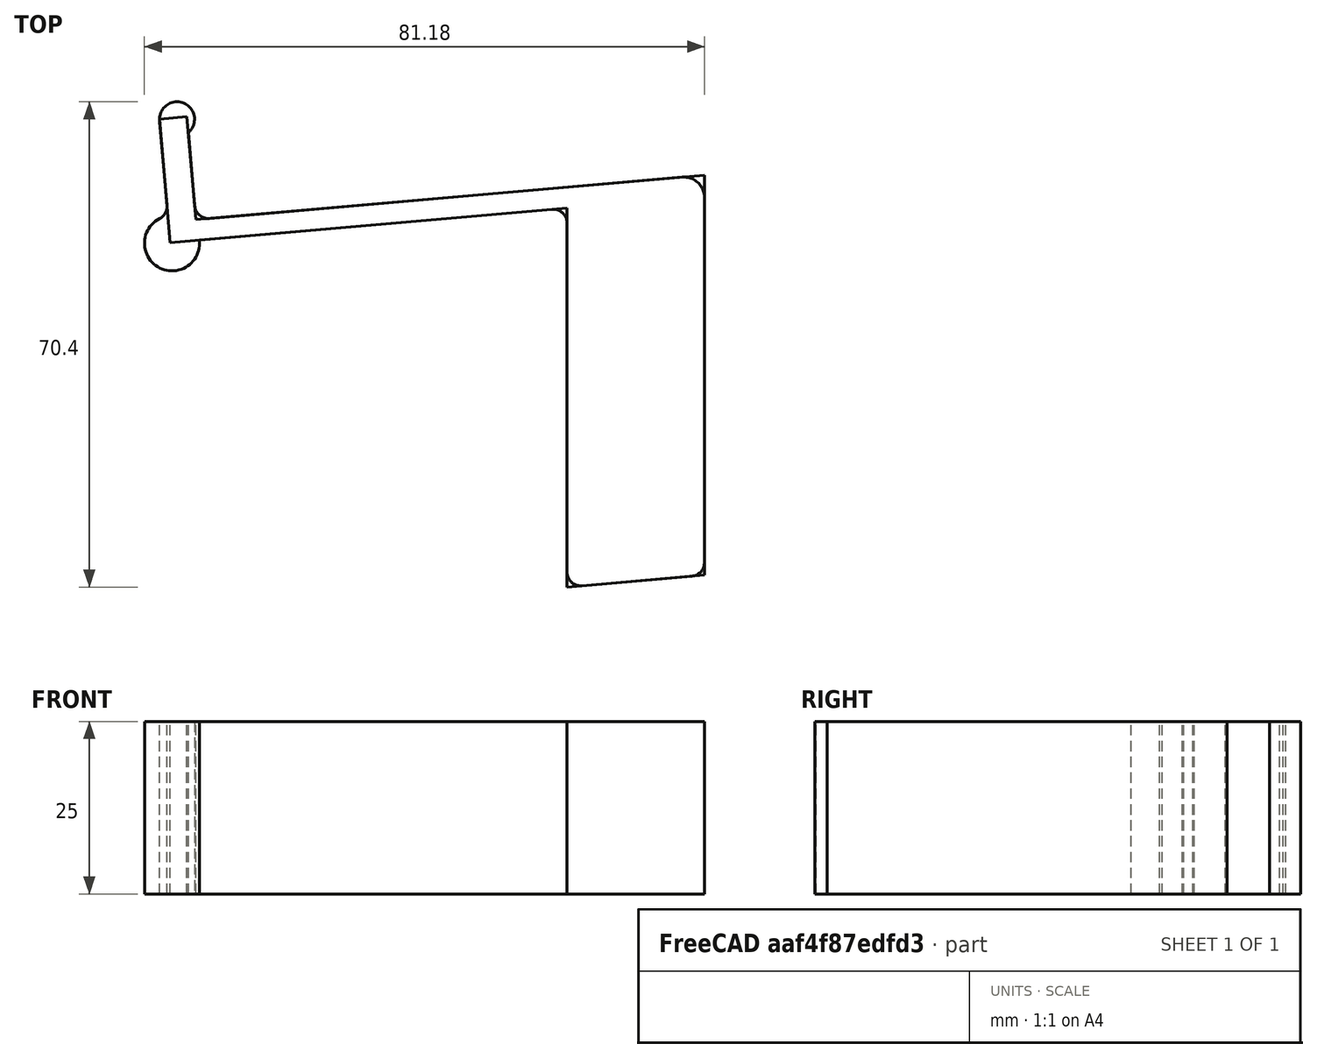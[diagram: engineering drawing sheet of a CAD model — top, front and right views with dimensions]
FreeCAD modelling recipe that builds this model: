
FCSTD DOCUMENT  (FreeCAD 0.16R)
Label: Hooks6
License: All rights reserved
LicenseURL: http://en.wikipedia.org/wiki/All_rights_reserved
objects: Sketcher::SketchObject×2, PartDesign::Pad×2, PartDesign::Fillet×2, Mesh::Feature×1
note: 8 computed .brp shape members not serialized (recipe doc carries the construction recipe); baked Part::Feature solids carry a one-line shape summary decoded from their .brp

FEATURE [Sketcher::SketchObject] Sketch
  sketch-geometry (9):
    g0: LineSegment StartX=19.9229 StartY=1.75449 StartZ=0 EndX=0 EndY=0 EndZ=0
    g1: LineSegment StartX=0 StartY=0 StartZ=0 EndX=0 EndY=55 EndZ=0
    g2: LineSegment StartX=0 StartY=55 StartZ=0 EndX=-57.5188 EndY=49.9678 EndZ=0
    g3: LineSegment StartX=-57.5188 StartY=49.9678 StartZ=0 EndX=-59.0876 EndY=67.8993 EndZ=0
    g4: LineSegment StartX=-59.0876 StartY=67.8993 StartZ=0 EndX=-55.1028 EndY=68.2479 EndZ=0
    g5: LineSegment StartX=-55.1028 StartY=68.2479 StartZ=0 EndX=-53.7955 EndY=53.305 EndZ=0
    g6: LineSegment StartX=-53.7955 StartY=53.305 StartZ=0 EndX=19.9229 EndY=59.7545 EndZ=0
    g7: LineSegment StartX=19.9229 StartY=59.7545 StartZ=0 EndX=19.9229 EndY=56.7545 EndZ=0
    g8: LineSegment StartX=19.9229 StartY=1.75449 StartZ=0 EndX=19.9229 EndY=56.7545 EndZ=0
  constraints (27):
    c: PointOnObject(g0,g-1)
    c: Coincident(g0,g1)
    c: Vertical(g1)
    c: Coincident(g1,g2)
    c: Coincident(g2,g3)
    c: Coincident(g3,g4)
    c: Coincident(g4,g5)
    c: Coincident(g5,g6)
    c: Angle(g2) = -3.05433
    c: Distance(g5) = 15
    c: Distance(g6) = 74
    c: Perpendicular(g3,g2)
    c: Parallel(g4,g2)
    c: Parallel(g5,g3)
    c: Distance(g4) = 4
    c: Distance(g5,g2) = 3
    c: Parallel(g6,g2)
    c: Distance(g1) = 55
    c: Vertical(g7)
    c: DistanceY(g7,g7) = 3
    c: Vertical(g8)
    c: Coincident(g6,g7)
    c: Distance(g1,g7) = 20
    c: Coincident(g8,g7)
    c: Coincident(g0,g8)
    c: Distance(g8) = 55
    c: Coincident(g0,g-1)
FEATURE [PartDesign::Pad] Pad
  Length = 25
  Length2 = 100
  Sketch = -> Sketch
  Type = 0
FEATURE [Sketcher::SketchObject] Sketch001
  Placement = pos=(0,0,25) rot=(0,0,1;0rad)
  Support = -> Pad [Face11]
  sketch-geometry (2):
    g0: Circle CenterX=-57.2592 CenterY=49.8759 CenterZ=0 NormalX=0 NormalY=0 NormalZ=1 Radius=4
    g1: Circle CenterX=-56.5462 CenterY=67.862 CenterZ=0 NormalX=0 NormalY=0 NormalZ=1 Radius=2.53997
  constraints (1):
    c: Radius(g0) = 4
FEATURE [PartDesign::Pad] Pad001
  Length = 25
  Length2 = 100
  Reversed = true
  Sketch = -> Sketch001
  Type = 0
FEATURE [PartDesign::Fillet] Fillet
  Base = -> Pad001 [Edge27,Edge34,Edge8,Edge2,Edge1]
  Radius = 2
FEATURE [PartDesign::Fillet] Fillet001
  Base = -> Fillet [Edge36]
  Radius = 3
FEATURE [Mesh::Feature] Mesh  label="Fillet001 (Meshed)"
